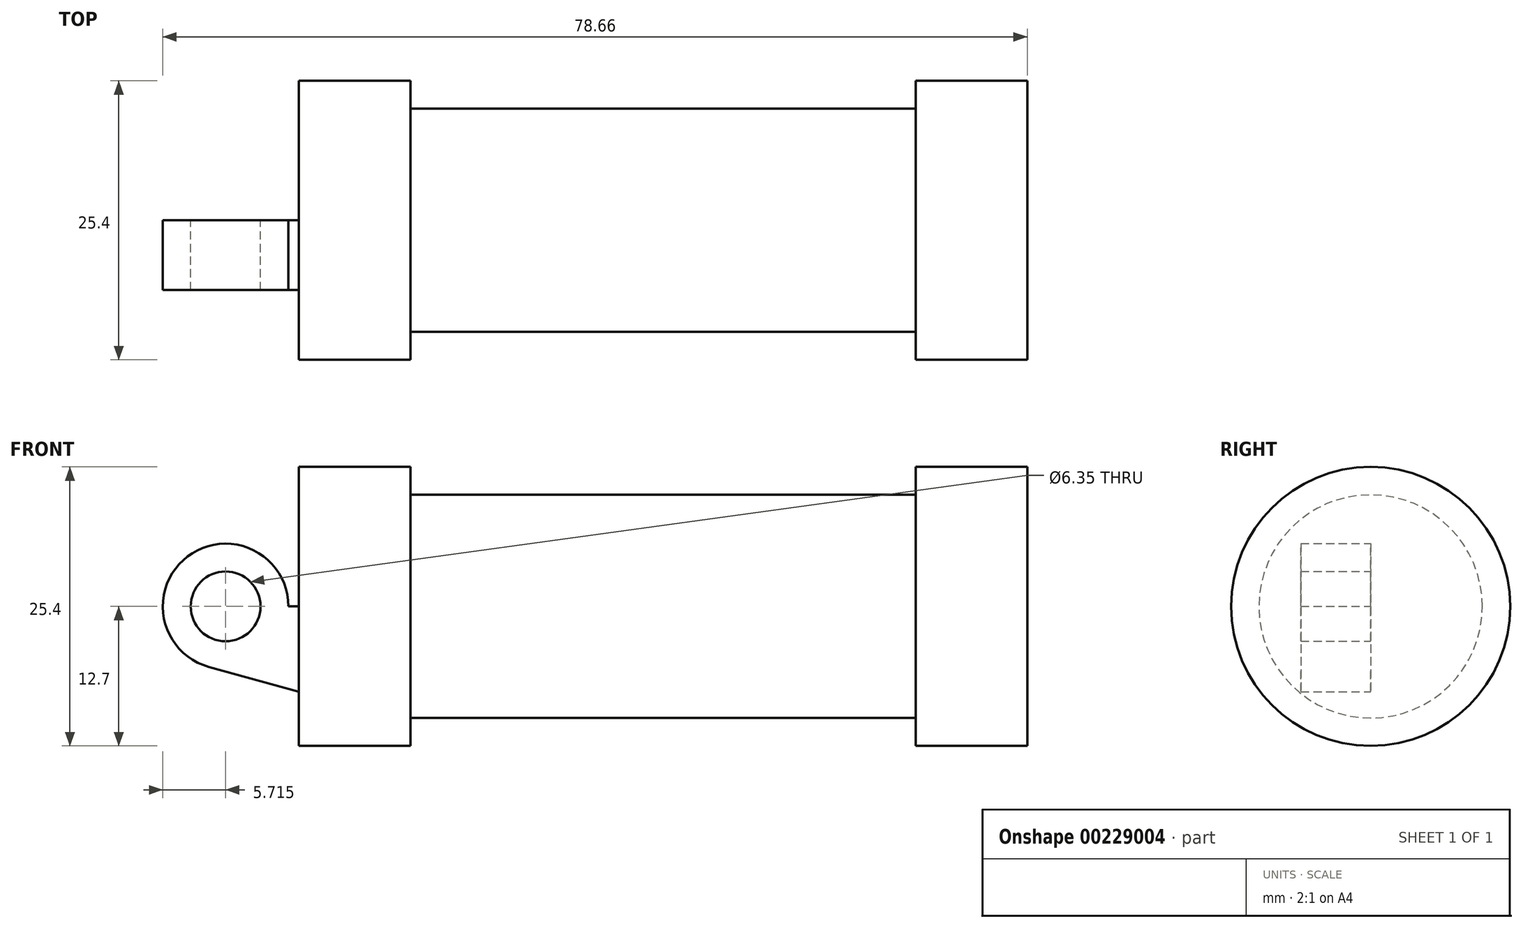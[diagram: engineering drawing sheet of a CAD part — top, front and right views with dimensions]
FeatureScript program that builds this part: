
annotation { "Feature Type Name" : "Feature", "Feature Type Description" : "" }
export const myFeature = defineFeature(function(context is Context, id is Id, definition is map)
    precondition{}
    {
        {
            var Q0;
            Q0=qCreatedBy(makeId("Front.planeOp"),FACE);
            var sketch = newSketch(context, id + "F0", { "sketchPlane" : qUnion([Q0])});
            skLineSegment(sketch, "E0", {"start": v(0, 0) * mm, "end": v(0, 12.7) * mm});
            skLineSegment(sketch, "E1", {"start": v(0, 12.7) * mm, "end": v(10.16, 12.7) * mm});
            skLineSegment(sketch, "E2", {"start": v(10.16, 12.7) * mm, "end": v(10.16, 10.16) * mm});
            skLineSegment(sketch, "E3", {"start": v(10.16, 10.16) * mm, "end": v(56.13, 10.16) * mm});
            skLineSegment(sketch, "E4", {"start": v(56.13, 10.16) * mm, "end": v(56.13, 12.7) * mm});
            skLineSegment(sketch, "E5", {"start": v(56.13, 12.7) * mm, "end": v(66.3, 12.7) * mm});
            skLineSegment(sketch, "E6", {"start": v(66.3, 12.7) * mm, "end": v(66.3, 0) * mm});
            skLineSegment(sketch, "E7", {"start": v(66.3, 0) * mm, "end": v(0, 0) * mm});
            skLineSegment(sketch, "E8", {"start": v(5.84, 15.24) * mm, "end": v(-0.5, 15.24) * mm});
            skLineSegment(sketch, "E9", {"start": v(-0.5, 15.24) * mm, "end": v(-10.88, 3.85) * mm});
            skLineSegment(sketch, "E10", {"start": v(0, 0) * mm, "end": v(-6.65, 0) * mm});
            skCircle(sketch, "E11", {"center": v(-6.65, 0) * mm, "radius": 5.72 * mm});
            skCircle(sketch, "E12", {"center": v(-6.65, 0) * mm, "radius": 3.18 * mm});
            skLineSegment(sketch, "E13", {"start": v(5.84, 15.24) * mm, "end": v(5.84, -9.4) * mm});
            skLineSegment(sketch, "E14", {"start": v(5.84, -9.4) * mm, "end": v(-8.18, -5.5) * mm});
            skSolve(sketch);
        }
        {
            var Q0;
            {var subQ0=sQuery(id+"F0.wireOp",EDGE,"E0");Q0=makeQuery(id+"F0.imprint","IMPRINT",FACE,{"disambiguationData":[TD([[makeQuery(id+"F0.imprint","IMPRINT",EDGE,{"derivedFrom":subQ0}),-1.0]])]});}
            var Q1;
            Q1=sQuery(id+"F0.wireOp",EDGE,"E7");
            revolve(context, id + "F1", {"entities" : qUnion([Q0]), "axis" : qUnion([Q1]), "revolveType" : RevolveType.FULL});
        }
        {
            var Q0;
            {var subQ0=sQuery(id+"F0.wireOp",EDGE,"E2");Q0=makeQuery(id+"F0.imprint","IMPRINT",FACE,{"disambiguationData":[TD([[makeQuery(id+"F0.imprint","IMPRINT",EDGE,{"derivedFrom":subQ0}),-1.0]])]});}
            var Q1;
            Q1=sQuery(id+"F0.wireOp",EDGE,"E7");
            revolve(context, id + "F2", {"operationType" : NewBodyOperationType.ADD, "entities" : qUnion([Q0]), "axis" : qUnion([Q1]), "revolveType" : RevolveType.FULL});
        }
        {
            var Q0;
            {var subQ4=sQuery(id+"F0.wireOp",EDGE,"E12");Q0=makeQuery(id+"F0.imprint","IMPRINT",FACE,{"disambiguationData":[TD([[makeQuery(id+"F0.imprint","IMPRINT",EDGE,{"derivedFrom":subQ4}),-1.0]])]});}
            var Q1;
            {var subQ0=sQuery(id+"F0.wireOp",EDGE,"E14");Q1=makeQuery(id+"F0.imprint","IMPRINT",FACE,{"disambiguationData":[TD([[makeQuery(id+"F0.imprint","IMPRINT",EDGE,{"derivedFrom":subQ0}),-1.0]])]});}
            extrude(context, id + "F3", {"entities" : qUnion([Q0, Q1]), "operationType" : NewBodyOperationType.ADD, "depth" : 6.35 * mm});
        }
    });
